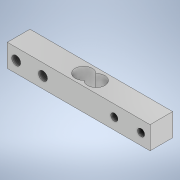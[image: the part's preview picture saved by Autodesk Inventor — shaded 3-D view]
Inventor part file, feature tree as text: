
AUTODESK INVENTOR PART (.ipt)
format: ipt  version: 2021 (Build 250183000, 183)  size: 134,656 bytes
history: native  units: mm
features: other x5, extrude x2, sketch x2
ambient origin geometry x8: Origin, YZ Plane, XZ Plane, XY Plane, X Axis, Y Axis, Z Axis, Center Point
bodies: Body1 (feature_tree)
feature tree (9):
  other  "솔리드1"
  extrude  "돌출1"  Depth=80.0mm
  extrude  "돌출2"  Depth=12.7mm
  other  "스레드1"
  other  "스레드2"
  other  "스레드3"
  other  "스레드4"
  sketch  "스케치1"
  sketch  "스케치2"
